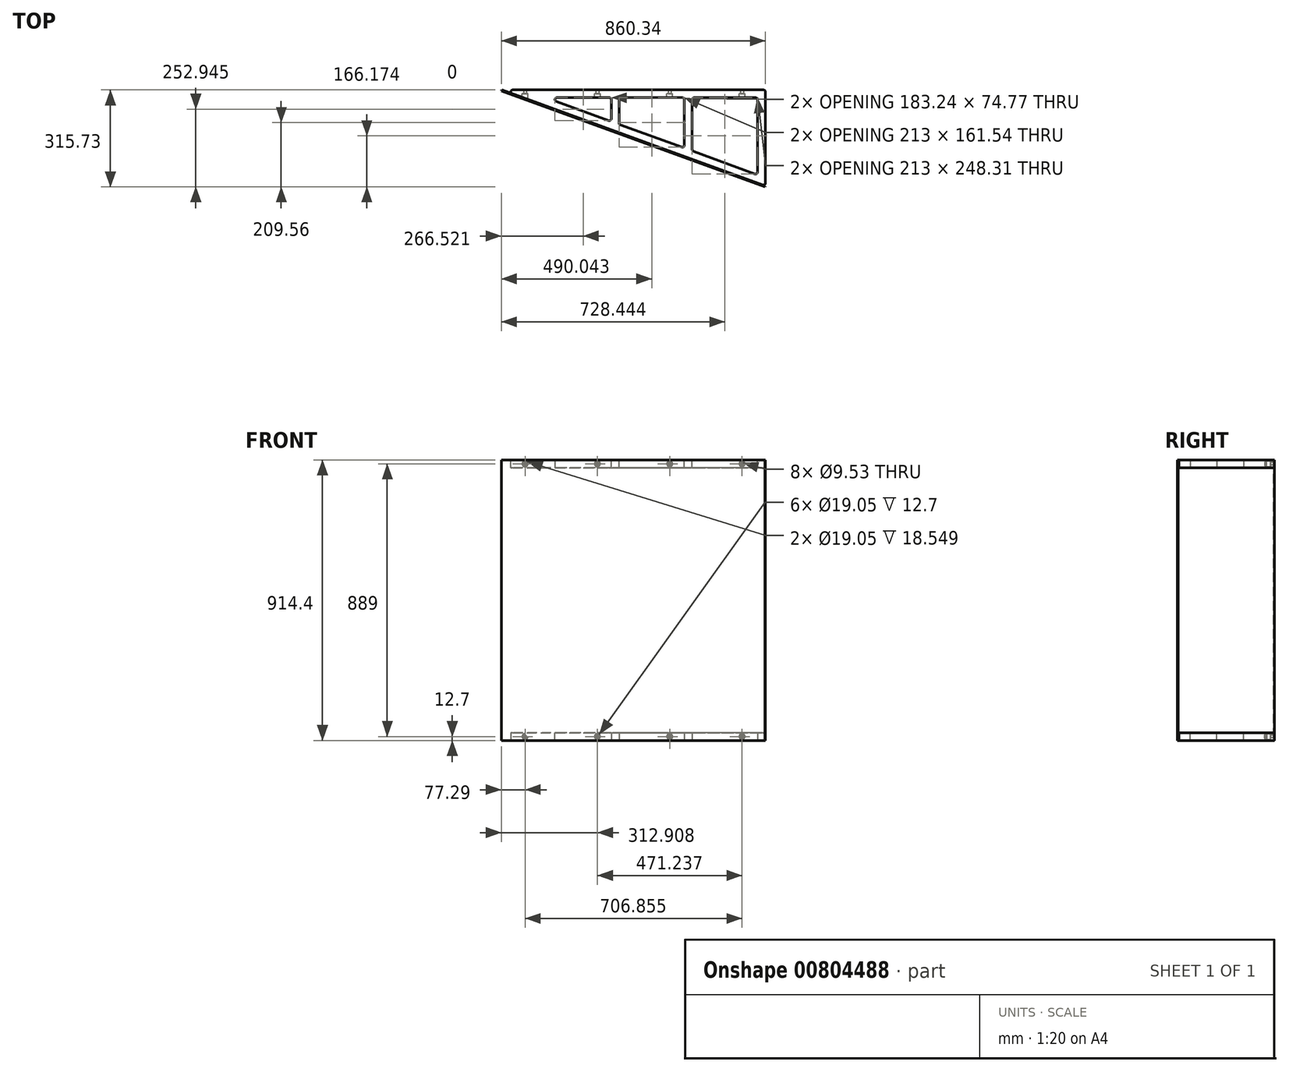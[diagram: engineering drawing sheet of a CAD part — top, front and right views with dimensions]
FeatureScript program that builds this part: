
annotation { "Feature Type Name" : "Feature", "Feature Type Description" : "" }
export const myFeature = defineFeature(function(context is Context, id is Id, definition is map)
    precondition{}
    {
        {
            assignVariable(context, id + "F0", {"name" : "T", "anyValue" : 25.4 * mm});
        }
        {
            assignVariable(context, id + "F1", {"name" : "V", "anyValue" : 914.4 * mm});
        }
        {
            var Q0;
            Q0=qCreatedBy(makeId("Top.planeOp"),FACE);
            cPlane(context, id + "F2", {"entities" : qUnion([Q0]), "cplaneType" : CPlaneType.OFFSET, "offset" : getVariable(context, 'V') / 2, "width" : 152.4 * mm, "height" : 152.4 * mm});
        }
        {
            var Q0;
            Q0=qCreatedBy(id+"F2.planeOp",FACE);
            var sketch = newSketch(context, id + "F3", { "sketchPlane" : qUnion([Q0])});
            skLineSegment(sketch, "E0", {"start": v(859.25, -312.74) * mm, "end": v(0, 0) * mm});
            skLineSegment(sketch, "E1", {"start": v(0, 0) * mm, "end": v(859.25, 0) * mm});
            skLineSegment(sketch, "E2", {"start": v(859.25, 0) * mm, "end": v(859.25, -312.74) * mm});
            skSolve(sketch);
        }
        {
            var Q0;
            Q0=qSketchRegion(id+"F3",true);
            extrude(context, id + "F4", {"entities" : qUnion([Q0]), "oppositeDirection" : true, "depth" : getVariable(context, 'T')});
        }
        {
            var Q0;
            Q0=makeQuery(id+"F4.opExtrude","CAP_FACE",FACE,{"disambiguationData":[OSD([sQuery(id+"F3.wireOp",EDGE,"E0"),sQuery(id+"F3.wireOp",EDGE,"E1"),sQuery(id+"F3.wireOp",EDGE,"E2")])],"isStart":true});
            var sketch = newSketch(context, id + "F5", { "sketchPlane" : qUnion([Q0])});
            skLineSegment(sketch, "E3.0", {"start": v(833.85, -276.47) * mm, "end": v(833.85, -25.4) * mm});
            skLineSegment(sketch, "E3.1", {"start": v(833.85, -25.4) * mm, "end": v(144.05, -25.4) * mm});
            skLineSegment(sketch, "E3.2", {"start": v(144.05, -25.4) * mm, "end": v(833.85, -276.47) * mm});
            skLineSegment(sketch, "E4", {"start": v(357.05, -102.93) * mm, "end": v(357.05, -25.4) * mm});
            skLineSegment(sketch, "E5", {"start": v(382.45, -25.4) * mm, "end": v(382.45, -112.17) * mm});
            skLineSegment(sketch, "E6", {"start": v(595.45, -189.7) * mm, "end": v(595.45, -25.4) * mm});
            skLineSegment(sketch, "E7", {"start": v(620.85, -25.4) * mm, "end": v(620.85, -198.94) * mm});
            skLineSegment(sketch, "E8", {"start": v(144.05, -102.93) * mm, "end": v(357.05, -102.93) * mm, "construction": true});
            skLineSegment(sketch, "E9", {"start": v(382.45, -112.17) * mm, "end": v(595.45, -112.17) * mm, "construction": true});
            skLineSegment(sketch, "E10", {"start": v(620.85, -198.94) * mm, "end": v(833.85, -198.94) * mm, "construction": true});
            skSolve(sketch);
        }
        {
            var Q0;
            {var subQ3=sQuery(id+"F5.wireOp",EDGE,"E4");Q0=makeQuery(id+"F5.imprint","IMPRINT",FACE,{"disambiguationData":[TD([[makeQuery(id+"F5.imprint","IMPRINT",EDGE,{"derivedFrom":subQ3}),1.0]])]});}
            var Q1;
            {var subQ0=sQuery(id+"F5.wireOp",EDGE,"E5");Q1=makeQuery(id+"F5.imprint","IMPRINT",FACE,{"disambiguationData":[TD([[makeQuery(id+"F5.imprint","IMPRINT",EDGE,{"derivedFrom":subQ0}),1.0]])]});}
            var Q2;
            {var subQ0=sQuery(id+"F5.wireOp",EDGE,"E3.0");Q2=makeQuery(id+"F5.imprint","IMPRINT",FACE,{"disambiguationData":[TD([[makeQuery(id+"F5.imprint","IMPRINT",EDGE,{"derivedFrom":subQ0}),1.0]])]});}
            extrude(context, id + "F6", {"entities" : qUnion([Q0, Q1, Q2]), "operationType" : NewBodyOperationType.REMOVE, "endBound" : BoundingType.THROUGH_ALL, "oppositeDirection" : true, "depth" : 25.4 * mm});
        }
        {
            var Q0;
            Q0=makeQuery(id+"F4.opExtrude","SWEPT_EDGE",EDGE,{"disambiguationData":[OSD([sQuery(id+"F3.wireOp",EDGE,"E0"),sQuery(id+"F3.wireOp",EDGE,"E1")])]});
            var Q1;
            Q1=makeQuery(id+"F4.opExtrude","SWEPT_EDGE",EDGE,{"disambiguationData":[OSD([sQuery(id+"F3.wireOp",EDGE,"E0"),sQuery(id+"F3.wireOp",EDGE,"E2")])]});
            var Q2;
            Q2=makeQuery(id+"F4.opExtrude","SWEPT_EDGE",EDGE,{"disambiguationData":[OSD([sQuery(id+"F3.wireOp",EDGE,"E1"),sQuery(id+"F3.wireOp",EDGE,"E2")])]});
            fillet(context, id + "F7", {"entities" : qUnion([Q0, Q1, Q2]), "radius" : 6.35 * mm, "tangentPropagation" : true, "allowEdgeOverflow" : false});
        }
        {
            var Q0;
            Q0=makeQuery(id+"F6.boolean.opBoolean","COPY",EDGE,{"derivedFrom":makeQuery(id+"F6.opExtrude","SWEPT_EDGE",EDGE,{"disambiguationData":[OSD([sQuery(id+"F5.wireOp",EDGE,"E3.1"),sQuery(id+"F5.wireOp",EDGE,"E3.2")])]})});
            var Q1;
            Q1=makeQuery(id+"F6.boolean.opBoolean","COPY",EDGE,{"derivedFrom":makeQuery(id+"F6.opExtrude","SWEPT_EDGE",EDGE,{"disambiguationData":[OSD([sQuery(id+"F5.wireOp",EDGE,"E3.2"),sQuery(id+"F5.wireOp",EDGE,"E5")])]})});
            var Q2;
            Q2=makeQuery(id+"F6.boolean.opBoolean","COPY",EDGE,{"derivedFrom":makeQuery(id+"F6.opExtrude","SWEPT_EDGE",EDGE,{"disambiguationData":[OSD([sQuery(id+"F5.wireOp",EDGE,"E3.1"),sQuery(id+"F5.wireOp",EDGE,"E5")])]})});
            var Q3;
            Q3=makeQuery(id+"F6.boolean.opBoolean","COPY",EDGE,{"derivedFrom":makeQuery(id+"F6.opExtrude","SWEPT_EDGE",EDGE,{"disambiguationData":[OSD([sQuery(id+"F5.wireOp",EDGE,"E3.1"),sQuery(id+"F5.wireOp",EDGE,"E7")])]})});
            var Q4;
            Q4=makeQuery(id+"F6.boolean.opBoolean","COPY",EDGE,{"derivedFrom":makeQuery(id+"F6.opExtrude","SWEPT_EDGE",EDGE,{"disambiguationData":[OSD([sQuery(id+"F5.wireOp",EDGE,"E3.2"),sQuery(id+"F5.wireOp",EDGE,"E7")])]})});
            var Q5;
            Q5=makeQuery(id+"F6.boolean.opBoolean","COPY",EDGE,{"derivedFrom":makeQuery(id+"F6.opExtrude","SWEPT_EDGE",EDGE,{"disambiguationData":[OSD([sQuery(id+"F5.wireOp",EDGE,"E3.1"),sQuery(id+"F5.wireOp",EDGE,"E4")])]})});
            var Q6;
            Q6=makeQuery(id+"F6.boolean.opBoolean","COPY",EDGE,{"derivedFrom":makeQuery(id+"F6.opExtrude","SWEPT_EDGE",EDGE,{"disambiguationData":[OSD([sQuery(id+"F5.wireOp",EDGE,"E3.1"),sQuery(id+"F5.wireOp",EDGE,"E6")])]})});
            var Q7;
            Q7=makeQuery(id+"F6.boolean.opBoolean","COPY",EDGE,{"derivedFrom":makeQuery(id+"F6.opExtrude","SWEPT_EDGE",EDGE,{"disambiguationData":[OSD([sQuery(id+"F5.wireOp",EDGE,"E3.0"),sQuery(id+"F5.wireOp",EDGE,"E3.1")])]})});
            var Q8;
            Q8=makeQuery(id+"F6.boolean.opBoolean","COPY",EDGE,{"derivedFrom":makeQuery(id+"F6.opExtrude","SWEPT_EDGE",EDGE,{"disambiguationData":[OSD([sQuery(id+"F5.wireOp",EDGE,"E3.2"),sQuery(id+"F5.wireOp",EDGE,"E4")])]})});
            var Q9;
            Q9=makeQuery(id+"F6.boolean.opBoolean","COPY",EDGE,{"derivedFrom":makeQuery(id+"F6.opExtrude","SWEPT_EDGE",EDGE,{"disambiguationData":[OSD([sQuery(id+"F5.wireOp",EDGE,"E3.2"),sQuery(id+"F5.wireOp",EDGE,"E6")])]})});
            var Q10;
            Q10=makeQuery(id+"F6.boolean.opBoolean","COPY",EDGE,{"derivedFrom":makeQuery(id+"F6.opExtrude","SWEPT_EDGE",EDGE,{"disambiguationData":[OSD([sQuery(id+"F5.wireOp",EDGE,"E3.0"),sQuery(id+"F5.wireOp",EDGE,"E3.2")])]})});
            fillet(context, id + "F8", {"entities" : qUnion([Q0, Q1, Q2, Q3, Q4, Q5, Q6, Q7, Q8, Q9, Q10]), "radius" : 6.35 * mm, "tangentPropagation" : true, "allowEdgeOverflow" : false});
        }
        {
            var Q0;
            Q0=qCreatedBy(makeId("Front.planeOp"),FACE);
            cPlane(context, id + "F9", {"entities" : qUnion([Q0]), "cplaneType" : CPlaneType.OFFSET, "offset" : getVariable(context, 'T') / 2, "width" : 152.4 * mm, "height" : 152.4 * mm});
        }
        {
            var Q0;
            Q0=qCreatedBy(id+"F9.planeOp",FACE);
            var sketch = newSketch(context, id + "F10", { "sketchPlane" : qUnion([Q0])});
            skLineSegment(sketch, "E11", {"start": v(783.05, 431.8) * mm, "end": v(783.05, 457.2) * mm, "construction": true});
            skCircle(sketch, "E12", {"center": v(783.05, 444.5) * mm, "radius": 9.53 * mm});
            skLineSegment(sketch, "E13", {"start": v(76.2, 444.5) * mm, "end": v(0, 444.5) * mm, "construction": true});
            skLineSegment(sketch, "E14", {"start": v(76.2, 444.5) * mm, "end": v(311.82, 444.5) * mm, "construction": true});
            skLineSegment(sketch, "E15", {"start": v(311.82, 444.5) * mm, "end": v(547.44, 444.5) * mm, "construction": true});
            skLineSegment(sketch, "E16", {"start": v(783.05, 444.5) * mm, "end": v(859.25, 444.5) * mm, "construction": true});
            skCircle(sketch, "E17", {"center": v(783.05, 444.5) * mm, "radius": 4.76 * mm});
            skCircle(sketch, "E18.1.0.0", {"center": v(547.44, 444.5) * mm, "radius": 9.53 * mm});
            skCircle(sketch, "E18.1.0.1", {"center": v(547.44, 444.5) * mm, "radius": 4.76 * mm});
            skCircle(sketch, "E18.2.0.0", {"center": v(311.82, 444.5) * mm, "radius": 9.53 * mm});
            skCircle(sketch, "E18.2.0.1", {"center": v(311.82, 444.5) * mm, "radius": 4.76 * mm});
            skCircle(sketch, "E18.3.0.0", {"center": v(76.2, 444.5) * mm, "radius": 9.53 * mm});
            skCircle(sketch, "E18.3.0.1", {"center": v(76.2, 444.5) * mm, "radius": 4.76 * mm});
            skLineSegment(sketch, "E18.direction1", {"start": v(783.05, 444.5) * mm, "end": v(547.44, 444.5) * mm, "construction": true});
            skSolve(sketch);
        }
        {
            var Q0;
            Q0=makeQuery(id+"F10.imprint","IMPRINT",FACE,{"disambiguationData":[TD([[makeQuery(id+"F10.imprint","IMPRINT",EDGE,{"derivedFrom":sQuery(id+"F10.wireOp",EDGE,"E18.3.0.1")}),-1.0]])]});
            var Q1;
            {var subQ0=sQuery(id+"F10.wireOp",EDGE,"E18.3.0.0");var subQ1=sQuery(id+"F5.wireOp",EDGE,"E3.2");var subQ2=sQuery(id+"F5.wireOp",EDGE,"E3.1");var subQ3=makeQuery(id+"F8.opFillet","BLEND_EDGE",EDGE,{"blendedFrom":[makeQuery(id+"F6.boolean.opBoolean","COPY",EDGE,{"derivedFrom":makeQuery(id+"F6.opExtrude","SWEPT_EDGE",EDGE,{"disambiguationData":[OSD([subQ2,subQ1])]})}),makeQuery(id+"F6.boolean.opBoolean","COPY",FACE,{"derivedFrom":makeQuery(id+"F6.opExtrude","SWEPT_FACE",FACE,{"disambiguationData":[OSD([subQ2]),TDD([makeQuery(id+"F5.imprint","IMPRINT",EDGE,{"disambiguationData":[TD([[makeQuery(id+"F5.imprint","INTERSECT",VERTEX,{"derivedFrom":[subQ2,subQ1]}),1.0]])],"derivedFrom":subQ2})])]})})],"blendedInto":[makeQuery(id+"F6.boolean.opBoolean","COPY",FACE,{"derivedFrom":makeQuery(id+"F6.opExtrude","SWEPT_FACE",FACE,{"disambiguationData":[OSD([subQ2]),TDD([makeQuery(id+"F5.imprint","IMPRINT",EDGE,{"disambiguationData":[TD([[makeQuery(id+"F5.imprint","INTERSECT",VERTEX,{"derivedFrom":[subQ2,subQ1]}),1.0]])],"derivedFrom":subQ2})])]})})]});var subQ4=makeQuery(id+"F10.imprint","INTERSECT",VERTEX,{"disambiguationData":[OD(0.0)],"derivedFrom":[subQ3,subQ0]});Q1=makeQuery(id+"F10.imprint","IMPRINT",FACE,{"disambiguationData":[TD([[makeQuery(id+"F10.imprint","IMPRINT",EDGE,{"disambiguationData":[TD([[subQ4,1.0]])],"derivedFrom":subQ0}),1.0]])]});}
            var Q2;
            Q2=makeQuery(id+"F10.imprint","IMPRINT",FACE,{"disambiguationData":[TD([[makeQuery(id+"F10.imprint","IMPRINT",EDGE,{"derivedFrom":sQuery(id+"F10.wireOp",EDGE,"E18.3.0.1")}),1.0]])]});
            var Q3;
            Q3=makeQuery(id+"F10.imprint","IMPRINT",FACE,{"disambiguationData":[TD([[makeQuery(id+"F10.imprint","IMPRINT",EDGE,{"derivedFrom":sQuery(id+"F10.wireOp",EDGE,"E18.2.0.1")}),1.0]])]});
            var Q4;
            Q4=makeQuery(id+"F10.imprint","IMPRINT",FACE,{"disambiguationData":[TD([[makeQuery(id+"F10.imprint","IMPRINT",EDGE,{"derivedFrom":sQuery(id+"F10.wireOp",EDGE,"E18.2.0.1")}),-1.0]])]});
            var Q5;
            {var subQ0=sQuery(id+"F10.wireOp",EDGE,"E18.2.0.0");var subQ1=sQuery(id+"F5.wireOp",EDGE,"E3.1");var subQ2=sQuery(id+"F5.wireOp",EDGE,"E4");var subQ3=makeQuery(id+"F8.opFillet","BLEND_EDGE",EDGE,{"blendedFrom":[makeQuery(id+"F6.boolean.opBoolean","COPY",EDGE,{"derivedFrom":makeQuery(id+"F6.opExtrude","SWEPT_EDGE",EDGE,{"disambiguationData":[OSD([subQ1,subQ2])]})}),makeQuery(id+"F6.boolean.opBoolean","COPY",FACE,{"derivedFrom":makeQuery(id+"F6.opExtrude","SWEPT_FACE",FACE,{"disambiguationData":[OSD([subQ1]),TDD([makeQuery(id+"F5.imprint","IMPRINT",EDGE,{"disambiguationData":[TD([[makeQuery(id+"F5.imprint","INTERSECT",VERTEX,{"derivedFrom":[subQ1,sQuery(id+"F5.wireOp",EDGE,"E3.2")]}),1.0]])],"derivedFrom":subQ1})])]})})],"blendedInto":[makeQuery(id+"F6.boolean.opBoolean","COPY",FACE,{"derivedFrom":makeQuery(id+"F6.opExtrude","SWEPT_FACE",FACE,{"disambiguationData":[OSD([subQ1]),TDD([makeQuery(id+"F5.imprint","IMPRINT",EDGE,{"disambiguationData":[TD([[makeQuery(id+"F5.imprint","INTERSECT",VERTEX,{"derivedFrom":[subQ1,sQuery(id+"F5.wireOp",EDGE,"E3.2")]}),1.0]])],"derivedFrom":subQ1})])]})})]});var subQ4=makeQuery(id+"F10.imprint","INTERSECT",VERTEX,{"disambiguationData":[OD(0.0)],"derivedFrom":[subQ3,subQ0]});Q5=makeQuery(id+"F10.imprint","IMPRINT",FACE,{"disambiguationData":[TD([[makeQuery(id+"F10.imprint","IMPRINT",EDGE,{"disambiguationData":[TD([[subQ4,1.0]])],"derivedFrom":subQ0}),1.0]])]});}
            var Q6;
            Q6=makeQuery(id+"F10.imprint","IMPRINT",FACE,{"disambiguationData":[TD([[makeQuery(id+"F10.imprint","IMPRINT",EDGE,{"derivedFrom":sQuery(id+"F10.wireOp",EDGE,"E18.1.0.1")}),1.0]])]});
            var Q7;
            Q7=makeQuery(id+"F10.imprint","IMPRINT",FACE,{"disambiguationData":[TD([[makeQuery(id+"F10.imprint","IMPRINT",EDGE,{"derivedFrom":sQuery(id+"F10.wireOp",EDGE,"E18.1.0.0")}),1.0]])]});
            var Q8;
            Q8=makeQuery(id+"F10.imprint","IMPRINT",FACE,{"disambiguationData":[TD([[makeQuery(id+"F10.imprint","IMPRINT",EDGE,{"derivedFrom":sQuery(id+"F10.wireOp",EDGE,"E12")}),1.0]])]});
            var Q9;
            Q9=makeQuery(id+"F10.imprint","IMPRINT",FACE,{"disambiguationData":[TD([[makeQuery(id+"F10.imprint","IMPRINT",EDGE,{"derivedFrom":sQuery(id+"F10.wireOp",EDGE,"E17")}),1.0]])]});
            extrude(context, id + "F11", {"entities" : qUnion([Q0, Q1, Q2, Q3, Q4, Q5, Q6, Q7, Q8, Q9]), "operationType" : NewBodyOperationType.REMOVE, "depth" : 38.1 * mm});
        }
        {
            var Q0;
            Q0=makeQuery(id+"F10.imprint","IMPRINT",FACE,{"disambiguationData":[TD([[makeQuery(id+"F10.imprint","IMPRINT",EDGE,{"derivedFrom":sQuery(id+"F10.wireOp",EDGE,"E18.3.0.1")}),1.0]])]});
            var Q1;
            Q1=makeQuery(id+"F10.imprint","IMPRINT",FACE,{"disambiguationData":[TD([[makeQuery(id+"F10.imprint","IMPRINT",EDGE,{"derivedFrom":sQuery(id+"F10.wireOp",EDGE,"E18.2.0.1")}),1.0]])]});
            var Q2;
            Q2=makeQuery(id+"F10.imprint","IMPRINT",FACE,{"disambiguationData":[TD([[makeQuery(id+"F10.imprint","IMPRINT",EDGE,{"derivedFrom":sQuery(id+"F10.wireOp",EDGE,"E18.1.0.1")}),1.0]])]});
            var Q3;
            Q3=makeQuery(id+"F10.imprint","IMPRINT",FACE,{"disambiguationData":[TD([[makeQuery(id+"F10.imprint","IMPRINT",EDGE,{"derivedFrom":sQuery(id+"F10.wireOp",EDGE,"E17")}),1.0]])]});
            extrude(context, id + "F12", {"entities" : qUnion([Q0, Q1, Q2, Q3]), "operationType" : NewBodyOperationType.REMOVE, "endBound" : BoundingType.THROUGH_ALL, "oppositeDirection" : true, "depth" : 25.4 * mm});
        }
        {
            var Q0;
            Q0=makeQuery(id+"F4.opExtrude","SWEPT_BODY",BODY,{"disambiguationData":[OSD([sQuery(id+"F3.wireOp",EDGE,"E0"),sQuery(id+"F3.wireOp",EDGE,"E1"),sQuery(id+"F3.wireOp",EDGE,"E2")])]});
            var Q1;
            Q1=qCreatedBy(makeId("Top.planeOp"),FACE);
            mirror(context, id + "F13", {"entities" : qUnion([Q0]), "mirrorPlane" : qUnion([Q1])});
        }
        {
            var Q0;
            Q0=makeQuery(id+"F4.opExtrude","SWEPT_FACE",FACE,{"disambiguationData":[OSD([sQuery(id+"F3.wireOp",EDGE,"E0")])]});
            var sketch = newSketch(context, id + "F14", { "sketchPlane" : qUnion([Q0])});
            skLineSegment(sketch, "E19.bottom", {"start": v(0, 457.2) * mm, "end": v(914.4, 457.2) * mm});
            skLineSegment(sketch, "E19.top", {"start": v(0, -457.2) * mm, "end": v(914.4, -457.2) * mm});
            skLineSegment(sketch, "E19.left", {"start": v(0, 457.2) * mm, "end": v(0, -457.2) * mm});
            skLineSegment(sketch, "E19.right", {"start": v(914.4, 457.2) * mm, "end": v(914.4, -457.2) * mm});
            skSolve(sketch);
        }
        {
            var Q0;
            Q0=qSketchRegion(id+"F14",true);
            extrude(context, id + "F15", {"entities" : qUnion([Q0]), "depth" : 3.17 * mm});
        }
    });
